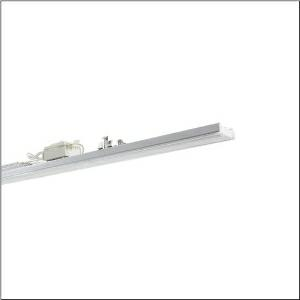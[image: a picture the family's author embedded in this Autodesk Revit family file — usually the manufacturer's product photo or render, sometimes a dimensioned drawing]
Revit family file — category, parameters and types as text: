
# Revit family: licross_r__11_recessed_ho_51tl18dv4m1m_dde3
name_source: partatom
category: Lighting Fixtures
units: mm (PartAtom-declared; Revit-internal decimal feet)

## family parameters
Cut with Voids When Loaded = No
Host = Face
Light Source = No
Part Type = Normal
Room Calculation Point = No
Round Connector Dimension = Use Diameter
Shared = No

## types (1)
- --- (1 x LED, 26860 lm, 150.5 W, 4000K)
    Apparent Load = 150 VA
    CIE Flux Codes = 78 94 99 100 100
    Color Rendering = 80
    Color Temperature = 4000K
    Default Elevation = 1800 mm
    Description = Licross® 11 Recessed HO, luminaire insert, of sheet steel, coil coated, white, length: 2.250mm, width: 66mm, height: 67mm, LED rated luminous flux: 26.870lm, light colour: 840, control gear: DALI 2, with plug, 5-pole, with phase selection, mains connection: 220..240V, AC, 50/60Hz, rated input power: 151W, internal wiring halogen-free, primary light control with lens, of plastic, primary optical cover: cover, of PMMA, light emission: direct distribution, primary light characteristic: symmetric, protection rating (complete): IP40, insulation class (complete): insulation class I (protective earthing), certification: CE, ENEC, VDE, UKCA, protection symbol: D if used in an environment without relevant dust loads with corresponding accessories, impact resistance: IK06, permissible ambient temperature for indoor applications: -40..+35°C, corresponds to IFS (International Featured Standards) requirements for safety and quality in the food industry, reducing of maximum allowable ambient temperature of 5°C with ceiling mounting, LABS conformity tested according to VDMA 24364:2018-05, packaging unit: 1 piece
    Height = 58 mm
    Lamp = 1 x LED
    Lamp Light Flux = 26860 lm
    Lamp Power = 150.5 W
    Lamp count = 1
    Length = 2250 mm
    Luminous efficacy = 178 lm/W
    Manufacturer = Siteco
    ModVariant = No
    Model = 51TL18DV4M1M
    Mounting Place = Ceiling
    Mounting Type = Pendant
    Number of Poles = 1
    OnlyDefault = Yes
    Power Factor = 1
    Product Name = Licross® 11 Recessed HO
    Product group = luminaire insert | ceiling pendant
    ProductGroupID = 902
    Protection Class = Protection class I
    Protection Degree = IP 40
    RLX_Detail_Level = 1
    RLX_Emergency_Light_Flux = 0 lm
    RLX_Emergency_Type = 0
    RLX_Emergency_Type_DB = No
    RlxData = <blob elided: 29653 chars, md5=297dd608>
    Socket = socket
    Standby Power = 0 W
    System Light Flux = 26860 lm
    System Power = 150 W
    Type Comments = factory setting: luminous flux: 100 % | dim-lin: 254 | 690 mA
    Type Image = l_1296930.jpg
    URL = http://relux.com
    VarID = @adj_120835
    Voltage = 0 V
    Weight = 0.00 kg
    Width = 66 mm

## geometry (parser evidence)
native form markers: Blend x4, Sweep x10
no freeform markers — native parametric forms only
